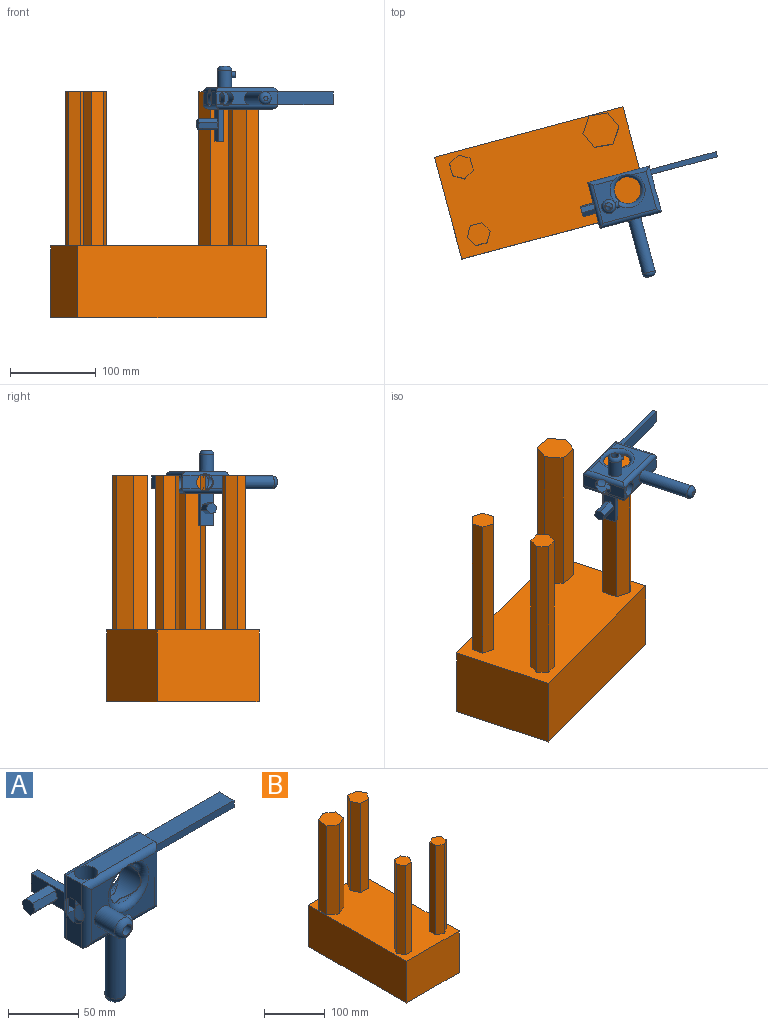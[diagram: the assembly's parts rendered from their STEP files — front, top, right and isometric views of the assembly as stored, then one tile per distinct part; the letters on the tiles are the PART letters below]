
ASSEMBLY  parts=2 mates=1
PART A: 56 faces, bbox 169.7x87.8x130.1 mm
  f0: plane 15x4.14mm, normal (1,0,0), area 62mm2, adj f1,f2,f3,f4
  f1: cylinder r=5mm len=55.63mm, axis (0,0,-1), area 385mm2, adj f0,f5,f6,f7,f8,f9,f10,f11
  f2: plane 79.8x15mm, normal (0,0,1), area 1197mm2, adj f0,f7,f12,f13
  f3: cylinder r=5mm len=55.63mm, axis (0,0,1), area 385mm2, adj f0,f5,f6,f11,f13,f14,f15,f16
  f4: plane 58.17x15mm, normal (0,0,1), area 824mm2, adj f0,f8,f16,f17
  f5: cylinder r=10mm len=74.38mm, axis (-1,0,0), area -128.2mm2, adj f1,f3,f6,f11,f17,f18,f19,f20
  f6: plane 15x10.24mm, normal (1,0,0), area 118.3mm2, adj f1,f3,f5,f30
  f7: plane 79.8x6.1mm, normal (0,-1,0), area 486.7mm2, adj f1,f2,f12,f30
  f8: cylinder r=5mm len=74.38mm, axis (1,0,0), area 508.8mm2, adj f1,f4,f9,f17,f19,f21,f31
  f9: plane 64.38x45.63mm, normal (0,-1,0), area 1488.6mm2, adj f1,f8,f10,f19,f21,f32
  f10: cylinder r=5mm len=74.38mm, axis (-1,0,0), area 550.5mm2, adj f1,f9,f21,f28,f33,f34,f35
  f11: plane 21.93x15mm, normal (1,0,0), area 293.7mm2, adj f1,f3,f5,f35
  f12: plane 15x6.1mm, normal (1,0,0), area 91.5mm2, adj f2,f7,f13,f30
  f13: plane 79.8x6.1mm, normal (0,1,0), area 486.7mm2, adj f2,f3,f12,f30
  f14: cylinder r=5mm len=74.38mm, axis (1,0,0), area 550.5mm2, adj f3,f15,f23,f28,f33,f34,f35
  f15: plane 64.38x45.63mm, normal (0,1,0), area 1594.8mm2, adj f3,f14,f16,f23,f26,f36,f37,f38
  f16: cylinder r=5mm len=74.38mm, axis (-1,0,0), area 508.8mm2, adj f3,f4,f15,f17,f23,f26,f31
  f17: cylinder r=8.47mm len=21.77mm, axis (0,0,1), area 1024.2mm2, adj f4,f5,f8,f16,f31
  f18: cylinder r=15.53mm len=31.06mm, axis (0,1,0), area -0.2mm2, adj f5
  f19: torus R=20.53mm, axis (0,-1,0), area 764.4mm2, adj f5,f8,f9,f20,f25
  f20: cylinder r=15.53mm len=17.47mm, axis (0,1,0), area 42.1mm2, adj f5,f19
  f21: cylinder r=5mm len=55.63mm, axis (0,0,1), area 385mm2, adj f5,f8,f9,f10,f22,f24
  f22: plane 21.93x15mm, normal (-1,0,0), area 293.7mm2, adj f5,f21,f23,f33
  f23: cylinder r=5mm len=55.63mm, axis (0,0,-1), area 385mm2, adj f5,f14,f15,f16,f22,f24
  f24: plane 20.47x15mm, normal (-1,0,0), area 271.9mm2, adj f5,f21,f23,f31
  f25: cylinder r=15.53mm len=31.05mm, axis (0,1,0), area 649.2mm2, adj f5,f19,f26
  f26: torus R=20.53mm, axis (0,-1,0), area 762.4mm2, adj f5,f15,f16,f25,f27
  f27: cylinder r=15.53mm len=17.47mm, axis (0,1,0), area 42.1mm2, adj f5,f26
  f28: cylinder r=8.47mm len=23.22mm, axis (0,0,1), area 1069.2mm2, adj f5,f10,f14,f29,f33,f34
  f29: cylinder r=4.49mm len=33.8mm, axis (0,-1,0), area 828.7mm2, adj f5,f28,f40
  f30: plane 79.8x15mm, normal (0,0,-1), area 1197mm2, adj f6,f7,f12,f13
  f31: plane 15x8.35mm, normal (0,0,1), area 76.7mm2, adj f8,f16,f17,f24
  f32: cylinder r=8.14mm len=20.19mm, axis (0,1,0), area 998.5mm2, adj f9,f40,f41,f42,f43
  f33: plane 15x8.35mm, normal (0,0,-1), area 76.7mm2, adj f10,f14,f22,f28
  f34: plane 25.59x15mm, normal (0,0,-1), area 246.9mm2, adj f10,f14,f28,f44
  f35: plane 32.59x15mm, normal (0,0,-1), area 400.4mm2, adj f10,f11,f14,f44
  f36: plane 37.8x15.6mm, normal (1,0,0), area 589.5mm2, adj f15,f37,f39,f45
  f37: plane 37.8x6.53mm, normal (0,0,1), area 246.9mm2, adj f15,f36,f38,f45
  f38: plane 37.8x15.6mm, normal (-1,0,0), area 476.3mm2, adj f15,f37,f39,f45,f46,f47,f48,f49
  f39: plane 37.8x6.53mm, normal (0,0,-1), area 246.9mm2, adj f15,f36,f38,f45
  f40: torus R=3.14mm, axis (0,-1,0), area 279.1mm2, adj f29,f32
  f41: cylinder r=3.56mm len=7.12mm, axis (-1,0,0), area 95.1mm2, adj f32,f42,f43,f52
  f42: plane 1.19x0.05mm, normal (-1,0,0), area 0mm2, adj f32,f41
  f43: plane 5.94x1.6mm, normal (-1,0,0), area 6.7mm2, adj f32,f41
  f44: cylinder r=7.5mm len=64.3mm, axis (0,0,1), area 3030.1mm2, adj f34,f35,f53
  f45: plane 15.6x6.53mm, normal (0,1,0), area 101.9mm2, adj f36,f37,f38,f39
  f46: plane 22.9x4.93mm, normal (0,0.75,0.67), area 151.2mm2, adj f38,f47,f51,f54
  f47: plane 22.9x6.47mm, normal (0,-0.2,0.98), area 151.2mm2, adj f38,f46,f48,f54
  f48: plane 22.9x6.27mm, normal (0,-0.95,0.31), area 151.2mm2, adj f38,f47,f49,f54
  f49: plane 22.9x4.93mm, normal (0,-0.75,-0.67), area 151.2mm2, adj f38,f48,f50,f54
  f50: plane 22.9x6.47mm, normal (0,0.2,-0.98), area 151.2mm2, adj f38,f49,f51,f54
  f51: plane 22.9x6.27mm, normal (0,0.95,-0.31), area 151.2mm2, adj f38,f46,f50,f54
  f52: plane 7.12x7.12mm, normal (1,0,0), area 39.9mm2, adj f41
  f53: torus R=2.5mm, axis (0,0,-1), area 280.4mm2, adj f44,f55
  f54: plane 12.93x12.54mm, normal (-1,0,0), area 113.2mm2, adj f46,f47,f48,f49,f50,f51
  f55: plane 5x5mm, normal (0,0,-1), area 19.6mm2, adj f53
PART B: 34 faces, bbox 123.2x227.8x263.9 mm
  f0: plane 227.82x123.2mm, normal (0,0,-1), area 28068mm2, adj f2,f3,f4,f5
  f1: plane 227.82x123.2mm, normal (0,0,1), area 24979.7mm2, adj f2,f3,f4,f5,f6,f7,f8,f9
  f2: plane 123.2x83.91mm, normal (0,-1,0), area 10337.7mm2, adj f0,f1,f3,f4
  f3: plane 227.82x83.91mm, normal (1,0,0), area 19116.8mm2, adj f0,f1,f2,f5
  f4: plane 227.82x83.91mm, normal (-1,0,0), area 19116.8mm2, adj f0,f1,f2,f5
  f5: plane 123.2x83.91mm, normal (0,1,0), area 10337.7mm2, adj f0,f1,f3,f4
  f6: plane 180x21.29mm, normal (-1,0.09,0), area 3848.1mm2, adj f1,f7,f11,f12
  f7: plane 180x17.47mm, normal (-0.58,-0.82,0), area 3848.1mm2, adj f1,f6,f8,f12
  f8: plane 180x19.41mm, normal (0.42,-0.91,0), area 3848.1mm2, adj f1,f7,f9,f12
  f9: plane 180x21.29mm, normal (1,-0.09,0), area 3848.1mm2, adj f1,f8,f10,f12
  f10: plane 180x17.47mm, normal (0.58,0.82,0), area 3848.1mm2, adj f1,f9,f11,f12
  f11: plane 180x19.41mm, normal (-0.42,0.91,0), area 3848.1mm2, adj f1,f6,f10,f12
  f12: plane 42.58x38.81mm, normal (0,0,1), area 1187.4mm2, adj f6,f7,f8,f9,f10,f11
  f13: plane 36.42x32.46mm, normal (0,0,1), area 863.9mm2, adj f14,f15,f16,f17,f18,f19
  f14: plane 180x15.32mm, normal (-0.84,0.54,0), area 3282.3mm2, adj f1,f13,f15,f18
  f15: plane 180x16.23mm, normal (-0.89,-0.46,0), area 3282.3mm2, adj f1,f13,f14,f16
  f16: plane 180x18.21mm, normal (-0.05,-1,0), area 3282.3mm2, adj f1,f13,f15,f17
  f17: plane 180x15.32mm, normal (0.84,-0.54,0), area 3282.3mm2, adj f1,f13,f16,f19
  f18: plane 180x18.21mm, normal (0.05,1,0), area 3282.3mm2, adj f1,f13,f14,f19
  f19: plane 180x16.23mm, normal (0.89,0.46,0), area 3282.3mm2, adj f1,f13,f17,f18
  f20: plane 28.8x24.94mm, normal (0,0,1), area 538.8mm2, adj f21,f22,f23,f24,f25,f26
  f21: plane 180x12.47mm, normal (0.87,0.5,0), area 2592.2mm2, adj f1,f20,f22,f25
  f22: plane 180x14.4mm, normal (0,1,0), area 2592.2mm2, adj f1,f20,f21,f23
  f23: plane 180x12.47mm, normal (-0.87,0.5,0), area 2592.2mm2, adj f1,f20,f22,f24
  f24: plane 180x12.47mm, normal (-0.87,-0.5,0), area 2592.2mm2, adj f1,f20,f23,f26
  f25: plane 180x12.47mm, normal (0.87,-0.5,0), area 2592.2mm2, adj f1,f20,f21,f26
  f26: plane 180x14.4mm, normal (0,-1,0), area 2592.2mm2, adj f1,f20,f24,f25
  f27: plane 27.7x23.98mm, normal (0,0,1), area 498.2mm2, adj f28,f29,f30,f31,f32,f33
  f28: plane 180x11.99mm, normal (-0.5,0.87,0), area 2492.5mm2, adj f1,f27,f29,f32
  f29: plane 180x13.85mm, normal (-1,0,0), area 2492.5mm2, adj f1,f27,f28,f30
  f30: plane 180x11.99mm, normal (-0.5,-0.87,0), area 2492.5mm2, adj f1,f27,f29,f31
  f31: plane 180x11.99mm, normal (0.5,-0.87,0), area 2492.5mm2, adj f1,f27,f30,f33
  f32: plane 180x11.99mm, normal (0.5,0.87,0), area 2492.5mm2, adj f1,f27,f28,f33
  f33: plane 180x13.85mm, normal (1,0,0), area 2492.5mm2, adj f1,f27,f31,f32
PLACE A rot(axis=(-0.98,-0.13,0.13),91deg) t=(2.53,159.72,201.7)mm
PLACE B rot(axis=(0,0,-1),75deg) t=(-138.55,362.38,12.35)mm
MATE cylindrical A.f18 <-> B.f13  axis (0,0,-1) through (18.96,170.56,209.2)mm
